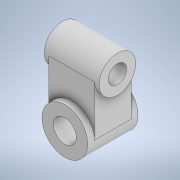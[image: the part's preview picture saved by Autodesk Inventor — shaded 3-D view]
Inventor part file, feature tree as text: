
AUTODESK INVENTOR PART (.ipt)
format: ipt  version: 2022.2 (Build 262287030, 287C)  size: 140,288 bytes
history: native  units: in
note: dims shown in document units (in); Inventor stores cm internally (conversion verified against a paired STEP export)
features: extrude x4, sketch x4, projected_geometry x2
ambient origin geometry x8: Origin, YZ Plane, XZ Plane, XY Plane, X Axis, Y Axis, Z Axis, Center Point
bodies: Solid1 (feature_tree)
feature tree (10):
  extrude  "Extrusion1"  Depth=1.25in
  extrude  "Extrusion2"  Depth=2.75in
  extrude  "Extrusion3"  Depth=1.0in
  extrude  "Extrusion4"  Depth=3.0in TaperAngle=0.0deg
  sketch  "Sketch1"  dims[d0=2.5in d1=1.25in]
  sketch  "Sketch2"  dims[d2=2.75in d3=0.0in d4=2.75in]
  sketch  "Sketch3"  dims[d5=2.0in d6=1.0in]
  projected_geometry  "Projected Loop1"
  projected_geometry  "Projected Loop2"
  sketch  "Sketch4"  dims[d7=3.0in d8=0.0in d9=3.0in d10=0.0in d11=0.0in d12=0.0in]
